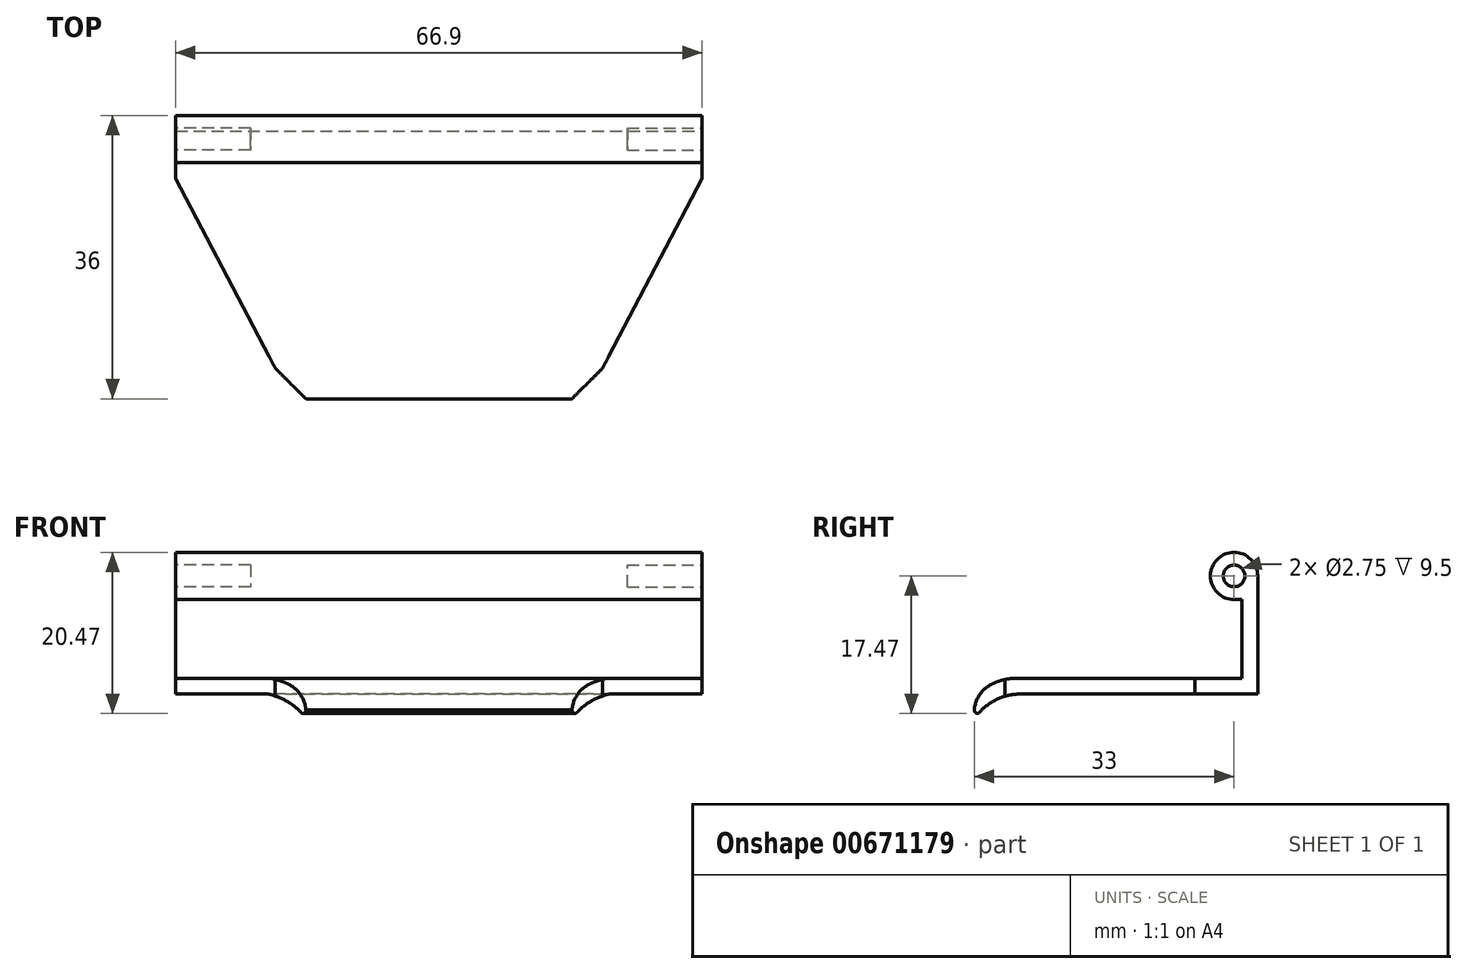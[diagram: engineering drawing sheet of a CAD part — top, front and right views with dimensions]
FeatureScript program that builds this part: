
annotation { "Feature Type Name" : "Feature", "Feature Type Description" : "" }
export const myFeature = defineFeature(function(context is Context, id is Id, definition is map)
    precondition{}
    {
        {
            var Q0;
            Q0=qCreatedBy(makeId("Top.planeOp"),FACE);
            var sketch = newSketch(context, id + "F0", { "sketchPlane" : qUnion([Q0])});
            skLineSegment(sketch, "E0.bottom", {"start": v(16.9, -21) * mm, "end": v(-16.9, -21) * mm});
            skLineSegment(sketch, "E0.top", {"start": v(33.45, 15) * mm, "end": v(-33.45, 15) * mm});
            skLineSegment(sketch, "E0.left", {"start": v(33.45, 7) * mm, "end": v(33.45, 15) * mm});
            skLineSegment(sketch, "E0.right", {"start": v(-33.45, 7) * mm, "end": v(-33.45, 15) * mm});
            skPoint(sketch, "E0.middle", {"position": v(0, 0) * mm});
            skLineSegment(sketch, "E1", {"start": v(-20.8, -17.1) * mm, "end": v(-16.9, -21) * mm});
            skLineSegment(sketch, "E2", {"start": v(20.8, -17.1) * mm, "end": v(16.9, -21) * mm});
            skLineSegment(sketch, "E3", {"start": v(-33.45, 7) * mm, "end": v(-20.8, -17.1) * mm});
            skLineSegment(sketch, "E4", {"start": v(33.45, 7) * mm, "end": v(20.8, -17.1) * mm});
            skSolve(sketch);
        }
        {
            var Q0;
            Q0 = qSketchRegion(id + "F0", true);
            extrude(context, id + "F1", {"entities" : qUnion([Q0]), "depth" : 2 * mm, "offsetDistance" : 25 * mm});
        }
        {
            var Q0;
            Q0=makeQuery(id+"F1.opExtrude","CAP_FACE",FACE,{"disambiguationData":[OSD([sQuery(id+"F0.wireOp",EDGE,"E0.bottom"),sQuery(id+"F0.wireOp",EDGE,"E0.top"),sQuery(id+"F0.wireOp",EDGE,"E0.left"),sQuery(id+"F0.wireOp",EDGE,"E0.right")])],"isStart":false});
            var sketch = newSketch(context, id + "F2", { "sketchPlane" : qUnion([Q0])});
            skLineSegment(sketch, "E5.bottom", {"start": v(-33.45, 15) * mm, "end": v(33.45, 15) * mm});
            skLineSegment(sketch, "E5.top", {"start": v(-33.45, 13) * mm, "end": v(33.45, 13) * mm});
            skLineSegment(sketch, "E5.left", {"start": v(-33.45, 15) * mm, "end": v(-33.45, 13) * mm});
            skLineSegment(sketch, "E5.right", {"start": v(33.45, 15) * mm, "end": v(33.45, 13) * mm});
            skSolve(sketch);
        }
        {
            var Q0;
            Q0 = qSketchRegion(id + "F2", true);
            extrude(context, id + "F3", {"entities" : qUnion([Q0]), "operationType" : NewBodyOperationType.ADD, "depth" : 16 * mm, "offsetDistance" : 25 * mm});
        }
        {
            var Q0;
            Q0=makeQuery(id+"F1.opExtrude","CAP_FACE",FACE,{"disambiguationData":[OSD([sQuery(id+"F0.wireOp",EDGE,"E0.bottom"),sQuery(id+"F0.wireOp",EDGE,"E0.top"),sQuery(id+"F0.wireOp",EDGE,"E0.left"),sQuery(id+"F0.wireOp",EDGE,"E0.right"),sQuery(id+"F0.wireOp",EDGE,"E1"),sQuery(id+"F0.wireOp",EDGE,"E2"),sQuery(id+"F0.wireOp",EDGE,"E3"),sQuery(id+"F0.wireOp",EDGE,"E4")])],"isStart":true});
            var sketch = newSketch(context, id + "F4", { "sketchPlane" : qUnion([Q0])});
            skLineSegment(sketch, "E6", {"start": v(-16.9, 21) * mm, "end": v(16.9, 21) * mm});
            skLineSegment(sketch, "E7", {"start": v(16.9, 21) * mm, "end": v(19.4, 18.5) * mm});
            skLineSegment(sketch, "E8", {"start": v(19.4, 18.5) * mm, "end": v(-19.4, 18.5) * mm});
            skLineSegment(sketch, "E9", {"start": v(-19.4, 18.5) * mm, "end": v(-16.9, 21) * mm});
            skSolve(sketch);
        }
        {
            var Q0;
            Q0 = qSketchRegion(id + "F4", true);
            extrude(context, id + "F5", {"entities" : qUnion([Q0]), "operationType" : NewBodyOperationType.ADD, "depth" : 2.5 * mm, "offsetDistance" : 25 * mm});
        }
        {
            var Q0;
            Q0=makeQuery(id+"F5.opExtrude","CAP_EDGE",EDGE,{"disambiguationData":[OSD([sQuery(id+"F4.wireOp",EDGE,"E8")])],"isStart":false});
            var Q1;
            Q1=makeQuery(id+"F1.opExtrude","CAP_EDGE",EDGE,{"disambiguationData":[OSD([sQuery(id+"F0.wireOp",EDGE,"E0.bottom")])],"isStart":false});
            chamfer(context, id + "F6", {"entities" : qUnion([Q0, Q1]), "chamferType" : ChamferType.TWO_OFFSETS, "width1" : 2.5 * mm, "oppositeDirection" : false, "width2" : 2 * mm, "tangentPropagation" : true});
        }
        {
            var Q0;
            Q0=makeQuery(id+"F6.opChamfer","BLEND_EDGE",EDGE,{"blendedFrom":[makeQuery(id+"F5.opExtrude","CAP_EDGE",EDGE,{"disambiguationData":[OSD([sQuery(id+"F4.wireOp",EDGE,"E8")])],"isStart":false}),makeQuery(id+"F1.opExtrude","CAP_FACE",FACE,{"disambiguationData":[OSD([sQuery(id+"F0.wireOp",EDGE,"E0.bottom"),sQuery(id+"F0.wireOp",EDGE,"E0.top"),sQuery(id+"F0.wireOp",EDGE,"E0.left"),sQuery(id+"F0.wireOp",EDGE,"E0.right"),sQuery(id+"F0.wireOp",EDGE,"E1"),sQuery(id+"F0.wireOp",EDGE,"E2"),sQuery(id+"F0.wireOp",EDGE,"E3"),sQuery(id+"F0.wireOp",EDGE,"E4")])],"isStart":true})],"blendedInto":[makeQuery(id+"F1.opExtrude","CAP_FACE",FACE,{"disambiguationData":[OSD([sQuery(id+"F0.wireOp",EDGE,"E0.bottom"),sQuery(id+"F0.wireOp",EDGE,"E0.top"),sQuery(id+"F0.wireOp",EDGE,"E0.left"),sQuery(id+"F0.wireOp",EDGE,"E0.right"),sQuery(id+"F0.wireOp",EDGE,"E1"),sQuery(id+"F0.wireOp",EDGE,"E2"),sQuery(id+"F0.wireOp",EDGE,"E3"),sQuery(id+"F0.wireOp",EDGE,"E4")])],"isStart":true})]});
            var Q1;
            {var subQ0=sQuery(id+"F0.wireOp",EDGE,"E0.bottom");Q1=makeQuery(id+"F6.opChamfer","BLEND_EDGE",EDGE,{"blendedFrom":[makeQuery(id+"F1.opExtrude","CAP_EDGE",EDGE,{"disambiguationData":[OSD([subQ0])],"isStart":false}),makeQuery(id+"F1.opExtrude","CAP_FACE",FACE,{"disambiguationData":[OSD([subQ0,sQuery(id+"F0.wireOp",EDGE,"E0.top"),sQuery(id+"F0.wireOp",EDGE,"E0.left"),sQuery(id+"F0.wireOp",EDGE,"E0.right"),sQuery(id+"F0.wireOp",EDGE,"E1"),sQuery(id+"F0.wireOp",EDGE,"E2"),sQuery(id+"F0.wireOp",EDGE,"E3"),sQuery(id+"F0.wireOp",EDGE,"E4")])],"isStart":false})],"blendedInto":[makeQuery(id+"F1.opExtrude","CAP_FACE",FACE,{"disambiguationData":[OSD([subQ0,sQuery(id+"F0.wireOp",EDGE,"E0.top"),sQuery(id+"F0.wireOp",EDGE,"E0.left"),sQuery(id+"F0.wireOp",EDGE,"E0.right"),sQuery(id+"F0.wireOp",EDGE,"E1"),sQuery(id+"F0.wireOp",EDGE,"E2"),sQuery(id+"F0.wireOp",EDGE,"E3"),sQuery(id+"F0.wireOp",EDGE,"E4")])],"isStart":false})]});}
            fillet(context, id + "F7", {"entities" : qUnion([Q0, Q1]), "radius" : 7 * mm, "tangentPropagation" : true, "allowEdgeOverflow" : false});
        }
        {
            var Q0;
            {var subQ0=sQuery(id+"F4.wireOp",EDGE,"E8");Q0=makeQuery(id+"F7.opFillet","BLEND_EDGE",EDGE,{"blendedFrom":[makeQuery(id+"F6.opChamfer","BLEND_EDGE",EDGE,{"blendedFrom":[makeQuery(id+"F5.opExtrude","CAP_EDGE",EDGE,{"disambiguationData":[OSD([subQ0])],"isStart":false}),makeQuery(id+"F1.opExtrude","CAP_FACE",FACE,{"disambiguationData":[OSD([sQuery(id+"F0.wireOp",EDGE,"E0.bottom"),sQuery(id+"F0.wireOp",EDGE,"E0.top"),sQuery(id+"F0.wireOp",EDGE,"E0.left"),sQuery(id+"F0.wireOp",EDGE,"E0.right"),sQuery(id+"F0.wireOp",EDGE,"E1"),sQuery(id+"F0.wireOp",EDGE,"E2"),sQuery(id+"F0.wireOp",EDGE,"E3"),sQuery(id+"F0.wireOp",EDGE,"E4")])],"isStart":true})],"blendedInto":[makeQuery(id+"F1.opExtrude","CAP_FACE",FACE,{"disambiguationData":[OSD([sQuery(id+"F0.wireOp",EDGE,"E0.bottom"),sQuery(id+"F0.wireOp",EDGE,"E0.top"),sQuery(id+"F0.wireOp",EDGE,"E0.left"),sQuery(id+"F0.wireOp",EDGE,"E0.right"),sQuery(id+"F0.wireOp",EDGE,"E1"),sQuery(id+"F0.wireOp",EDGE,"E2"),sQuery(id+"F0.wireOp",EDGE,"E3"),sQuery(id+"F0.wireOp",EDGE,"E4")])],"isStart":true})]}),makeQuery(id+"F5.opExtrude","CAP_FACE",FACE,{"disambiguationData":[OSD([sQuery(id+"F4.wireOp",EDGE,"E6"),sQuery(id+"F4.wireOp",EDGE,"E7"),subQ0,sQuery(id+"F4.wireOp",EDGE,"E9")])],"isStart":false})],"blendedInto":[makeQuery(id+"F5.opExtrude","CAP_FACE",FACE,{"disambiguationData":[OSD([sQuery(id+"F4.wireOp",EDGE,"E6"),sQuery(id+"F4.wireOp",EDGE,"E7"),subQ0,sQuery(id+"F4.wireOp",EDGE,"E9")])],"isStart":false})]});}
            var Q1;
            Q1=makeQuery(id+"F5.opExtrude","CAP_EDGE",EDGE,{"disambiguationData":[OSD([sQuery(id+"F4.wireOp",EDGE,"E6")])],"isStart":false});
            fillet(context, id + "F8", {"entities" : qUnion([Q0, Q1]), "radius" : .5 * mm, "tangentPropagation" : true, "allowEdgeOverflow" : false});
        }
        {
            var Q0;
            {var subQ0=sQuery(id+"F4.wireOp",EDGE,"E8");var subQ1=sQuery(id+"F4.wireOp",EDGE,"E6");Q0=makeQuery(id+"F8.opFillet","BLEND_EDGE",EDGE,{"blendedFrom":[makeQuery(id+"F5.opExtrude","CAP_EDGE",EDGE,{"disambiguationData":[OSD([subQ1])],"isStart":false}),makeQuery(id+"F7.opFillet","BLEND_EDGE",EDGE,{"blendedFrom":[makeQuery(id+"F6.opChamfer","BLEND_EDGE",EDGE,{"blendedFrom":[makeQuery(id+"F5.opExtrude","CAP_EDGE",EDGE,{"disambiguationData":[OSD([subQ0])],"isStart":false}),makeQuery(id+"F1.opExtrude","CAP_FACE",FACE,{"disambiguationData":[OSD([sQuery(id+"F0.wireOp",EDGE,"E0.bottom"),sQuery(id+"F0.wireOp",EDGE,"E0.top"),sQuery(id+"F0.wireOp",EDGE,"E0.left"),sQuery(id+"F0.wireOp",EDGE,"E0.right"),sQuery(id+"F0.wireOp",EDGE,"E1"),sQuery(id+"F0.wireOp",EDGE,"E2"),sQuery(id+"F0.wireOp",EDGE,"E3"),sQuery(id+"F0.wireOp",EDGE,"E4")])],"isStart":true})],"blendedInto":[makeQuery(id+"F1.opExtrude","CAP_FACE",FACE,{"disambiguationData":[OSD([sQuery(id+"F0.wireOp",EDGE,"E0.bottom"),sQuery(id+"F0.wireOp",EDGE,"E0.top"),sQuery(id+"F0.wireOp",EDGE,"E0.left"),sQuery(id+"F0.wireOp",EDGE,"E0.right"),sQuery(id+"F0.wireOp",EDGE,"E1"),sQuery(id+"F0.wireOp",EDGE,"E2"),sQuery(id+"F0.wireOp",EDGE,"E3"),sQuery(id+"F0.wireOp",EDGE,"E4")])],"isStart":true})]}),makeQuery(id+"F5.opExtrude","CAP_FACE",FACE,{"disambiguationData":[OSD([subQ1,sQuery(id+"F4.wireOp",EDGE,"E7"),subQ0,sQuery(id+"F4.wireOp",EDGE,"E9")])],"isStart":false})],"blendedInto":[makeQuery(id+"F5.opExtrude","CAP_FACE",FACE,{"disambiguationData":[OSD([subQ1,sQuery(id+"F4.wireOp",EDGE,"E7"),subQ0,sQuery(id+"F4.wireOp",EDGE,"E9")])],"isStart":false})]})],"blendedInto":[]});}
            fillet(context, id + "F9", {"entities" : qUnion([Q0]), "radius" : .25 * mm, "tangentPropagation" : true, "allowEdgeOverflow" : false});
        }
        {
            var Q0;
            {var subQ0=sQuery(id+"F0.wireOp",EDGE,"E0.bottom");Q0=makeQuery(id+"F7.opFillet","BLEND_EDGE",EDGE,{"blendedFrom":[makeQuery(id+"F6.opChamfer","BLEND_EDGE",EDGE,{"blendedFrom":[makeQuery(id+"F1.opExtrude","CAP_EDGE",EDGE,{"disambiguationData":[OSD([subQ0])],"isStart":false}),makeQuery(id+"F1.opExtrude","CAP_FACE",FACE,{"disambiguationData":[OSD([subQ0,sQuery(id+"F0.wireOp",EDGE,"E0.top"),sQuery(id+"F0.wireOp",EDGE,"E0.left"),sQuery(id+"F0.wireOp",EDGE,"E0.right"),sQuery(id+"F0.wireOp",EDGE,"E1"),sQuery(id+"F0.wireOp",EDGE,"E2"),sQuery(id+"F0.wireOp",EDGE,"E3"),sQuery(id+"F0.wireOp",EDGE,"E4")])],"isStart":false})],"blendedInto":[makeQuery(id+"F1.opExtrude","CAP_FACE",FACE,{"disambiguationData":[OSD([subQ0,sQuery(id+"F0.wireOp",EDGE,"E0.top"),sQuery(id+"F0.wireOp",EDGE,"E0.left"),sQuery(id+"F0.wireOp",EDGE,"E0.right"),sQuery(id+"F0.wireOp",EDGE,"E1"),sQuery(id+"F0.wireOp",EDGE,"E2"),sQuery(id+"F0.wireOp",EDGE,"E3"),sQuery(id+"F0.wireOp",EDGE,"E4")])],"isStart":false})]}),makeQuery(id+"F5.boolean.opBoolean","MERGE",FACE,{"derivedFrom":[makeQuery(id+"F1.opExtrude","SWEPT_FACE",FACE,{"disambiguationData":[OSD([subQ0])]}),makeQuery(id+"F5.opExtrude","SWEPT_FACE",FACE,{"disambiguationData":[OSD([sQuery(id+"F4.wireOp",EDGE,"E6")])]})]})],"blendedInto":[makeQuery(id+"F5.boolean.opBoolean","MERGE",FACE,{"derivedFrom":[makeQuery(id+"F1.opExtrude","SWEPT_FACE",FACE,{"disambiguationData":[OSD([subQ0])]}),makeQuery(id+"F5.opExtrude","SWEPT_FACE",FACE,{"disambiguationData":[OSD([sQuery(id+"F4.wireOp",EDGE,"E6")])]})]})]});}
            fillet(context, id + "F10", {"entities" : qUnion([Q0]), "radius" : 4 * mm, "tangentPropagation" : true, "allowEdgeOverflow" : false});
        }
        {
            var Q0;
            Q0=makeQuery(id+"F3.opExtrude","SWEPT_FACE",FACE,{"disambiguationData":[OSD([sQuery(id+"F2.wireOp",EDGE,"E5.top")])]});
            var sketch = newSketch(context, id + "F11", { "sketchPlane" : qUnion([Q0])});
            skLineSegment(sketch, "E10.bottom", {"start": v(-33.45, 18) * mm, "end": v(33.45, 18) * mm});
            skLineSegment(sketch, "E10.top", {"start": v(-33.45, 12) * mm, "end": v(33.45, 12) * mm});
            skLineSegment(sketch, "E10.left", {"start": v(-33.45, 18) * mm, "end": v(-33.45, 12) * mm});
            skLineSegment(sketch, "E10.right", {"start": v(33.45, 18) * mm, "end": v(33.45, 12) * mm});
            skSolve(sketch);
        }
        {
            var Q0;
            Q0 = qSketchRegion(id + "F11", true);
            extrude(context, id + "F12", {"entities" : qUnion([Q0]), "operationType" : NewBodyOperationType.ADD, "depth" : 4 * mm, "offsetDistance" : 25 * mm});
        }
        {
            var Q0;
            Q0=makeQuery(id+"F12.boolean.opBoolean","MERGE",FACE,{"derivedFrom":[makeQuery(id+"F3.boolean.opBoolean","MERGE",FACE,{"derivedFrom":[makeQuery(id+"F1.opExtrude","SWEPT_FACE",FACE,{"disambiguationData":[OSD([sQuery(id+"F0.wireOp",EDGE,"E0.left")])]}),makeQuery(id+"F3.opExtrude","SWEPT_FACE",FACE,{"disambiguationData":[OSD([sQuery(id+"F2.wireOp",EDGE,"E5.right")])]})]}),makeQuery(id+"F12.opExtrude","SWEPT_FACE",FACE,{"disambiguationData":[OSD([sQuery(id+"F11.wireOp",EDGE,"E10.right")])]})]});
            var sketch = newSketch(context, id + "F13", { "sketchPlane" : qUnion([Q0])});
            skCircle(sketch, "E11", {"center": v(12, 15) * mm, "radius": 1.38 * mm});
            skPoint(sketch, "E11.centerSnap0", {"position": v(12, 18) * mm});
            skPoint(sketch, "E11.centerSnap1", {"position": v(9, 15) * mm});
            skSolve(sketch);
        }
        {
            var Q0;
            Q0 = qSketchRegion(id + "F13", true);
            extrude(context, id + "F14", {"entities" : qUnion([Q0]), "operationType" : NewBodyOperationType.REMOVE, "oppositeDirection" : true, "depth" : 9.5 * mm, "offsetDistance" : 25 * mm});
        }
        {
            var Q0;
            Q0=makeQuery(id+"F12.boolean.opBoolean","MERGE",FACE,{"derivedFrom":[makeQuery(id+"F3.boolean.opBoolean","MERGE",FACE,{"derivedFrom":[makeQuery(id+"F1.opExtrude","SWEPT_FACE",FACE,{"disambiguationData":[OSD([sQuery(id+"F0.wireOp",EDGE,"E0.right")])]}),makeQuery(id+"F3.opExtrude","SWEPT_FACE",FACE,{"disambiguationData":[OSD([sQuery(id+"F2.wireOp",EDGE,"E5.left")])]})]}),makeQuery(id+"F12.opExtrude","SWEPT_FACE",FACE,{"disambiguationData":[OSD([sQuery(id+"F11.wireOp",EDGE,"E10.left")])]})]});
            var sketch = newSketch(context, id + "F15", { "sketchPlane" : qUnion([Q0])});
            skCircle(sketch, "E12", {"center": v(-12, 15) * mm, "radius": 1.38 * mm});
            skPoint(sketch, "E12.centerSnap0", {"position": v(-12, 18) * mm});
            skPoint(sketch, "E12.centerSnap1", {"position": v(-9, 15) * mm});
            skSolve(sketch);
        }
        {
            var Q0;
            Q0 = qSketchRegion(id + "F15", true);
            extrude(context, id + "F16", {"entities" : qUnion([Q0]), "operationType" : NewBodyOperationType.REMOVE, "oppositeDirection" : true, "depth" : 9.5 * mm, "offsetDistance" : 25 * mm});
        }
        {
            var Q0;
            Q0=makeQuery(id+"F12.opExtrude","CAP_EDGE",EDGE,{"disambiguationData":[OSD([sQuery(id+"F11.wireOp",EDGE,"E10.bottom")])],"isStart":false});
            var Q1;
            Q1=makeQuery(id+"F12.opExtrude","CAP_EDGE",EDGE,{"disambiguationData":[OSD([sQuery(id+"F11.wireOp",EDGE,"E10.top")])],"isStart":false});
            var Q2;
            Q2=makeQuery(id+"F3.opExtrude","CAP_EDGE",EDGE,{"disambiguationData":[OSD([sQuery(id+"F2.wireOp",EDGE,"E5.bottom")])],"isStart":false});
            fillet(context, id + "F17", {"entities" : qUnion([Q0, Q1, Q2]), "radius" : 3 * mm, "tangentPropagation" : true, "allowEdgeOverflow" : false});
        }
    });
